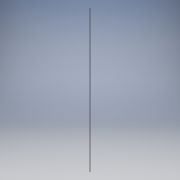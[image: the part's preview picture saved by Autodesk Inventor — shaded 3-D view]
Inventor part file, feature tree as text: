
AUTODESK INVENTOR PART (.ipt)
format: ipt  version: 2018 (Build 220112000, 112)  size: 98,304 bytes
history: native  units: mm
features: extrude x1, sketch x1
ambient origin geometry x8: Origin, YZ Plane, XZ Plane, XY Plane, X Axis, Y Axis, Z Axis, Center Point
bodies: Solid1 (feature_tree)
feature tree (2):
  extrude  "Extrusion1"  Depth=12.0mm
  sketch  "Sketch1"  dims[d0=6.0mm d1=12.0mm d2=4830.551mm d3=0.0mm]
